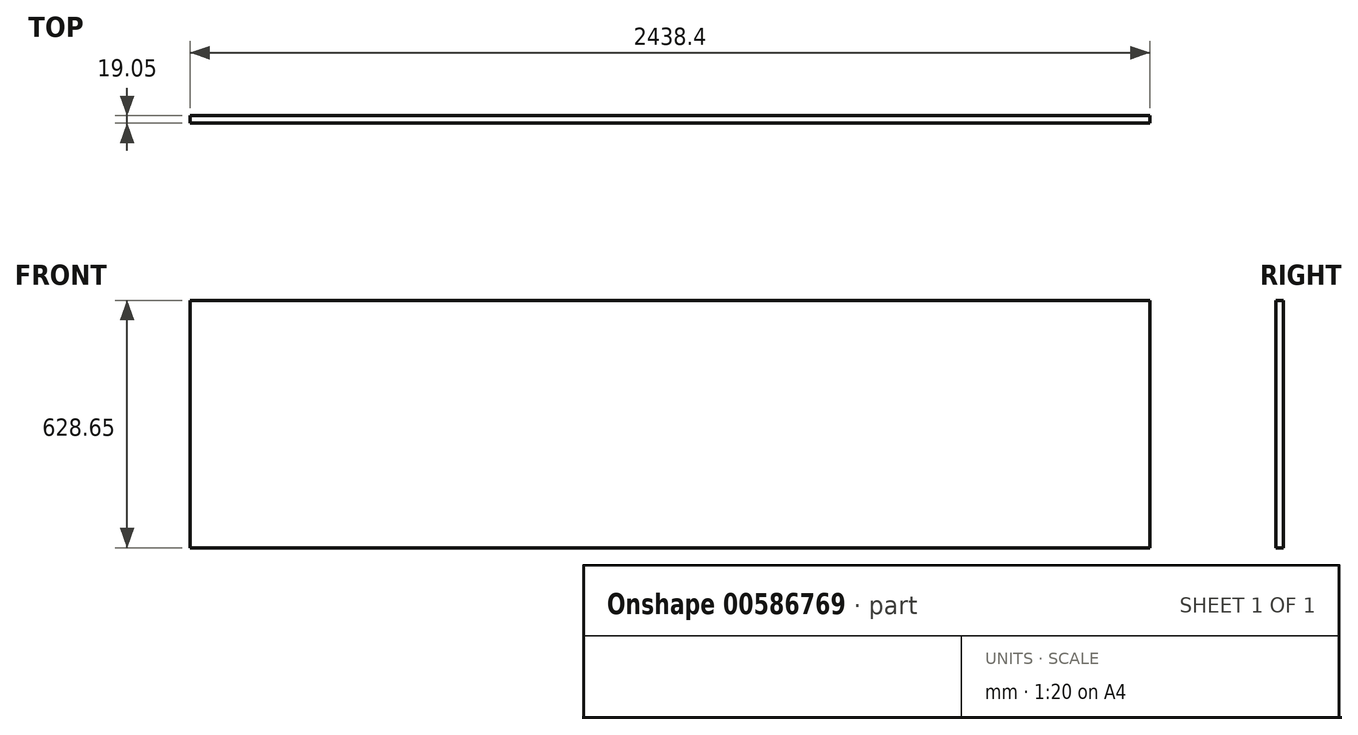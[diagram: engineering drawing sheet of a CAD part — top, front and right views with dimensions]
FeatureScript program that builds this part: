
annotation { "Feature Type Name" : "Feature", "Feature Type Description" : "" }
export const myFeature = defineFeature(function(context is Context, id is Id, definition is map)
    precondition{}
    {
        {
            var Q0;
            Q0=qCreatedBy(makeId("Front.planeOp"),FACE);
            var sketch = newSketch(context, id + "F0", { "sketchPlane" : qUnion([Q0])});
            skLineSegment(sketch, "E0.bottom", {"start": v(-915.71, 281.77) * mm, "end": v(1522.69, 281.77) * mm});
            skLineSegment(sketch, "E0.top", {"start": v(-915.71, -346.88) * mm, "end": v(1522.69, -346.88) * mm});
            skLineSegment(sketch, "E0.left", {"start": v(-915.71, 281.77) * mm, "end": v(-915.71, -346.88) * mm});
            skLineSegment(sketch, "E0.right", {"start": v(1522.69, 281.77) * mm, "end": v(1522.69, -346.88) * mm});
            skSolve(sketch);
        }
        {
            var Q0;
            Q0=makeQuery(id+"F0.imprint","IMPRINT",FACE,{"disambiguationData":[TD([[makeQuery(id+"F0.imprint","IMPRINT",EDGE,{"derivedFrom":sQuery(id+"F0.wireOp",EDGE,"E0.bottom")}),-1.0]])]});
            extrude(context, id + "F1", {"entities" : qUnion([Q0]), "depth" : 19.05 * mm, "offsetDistance" : 25.4 * mm});
        }
    });
